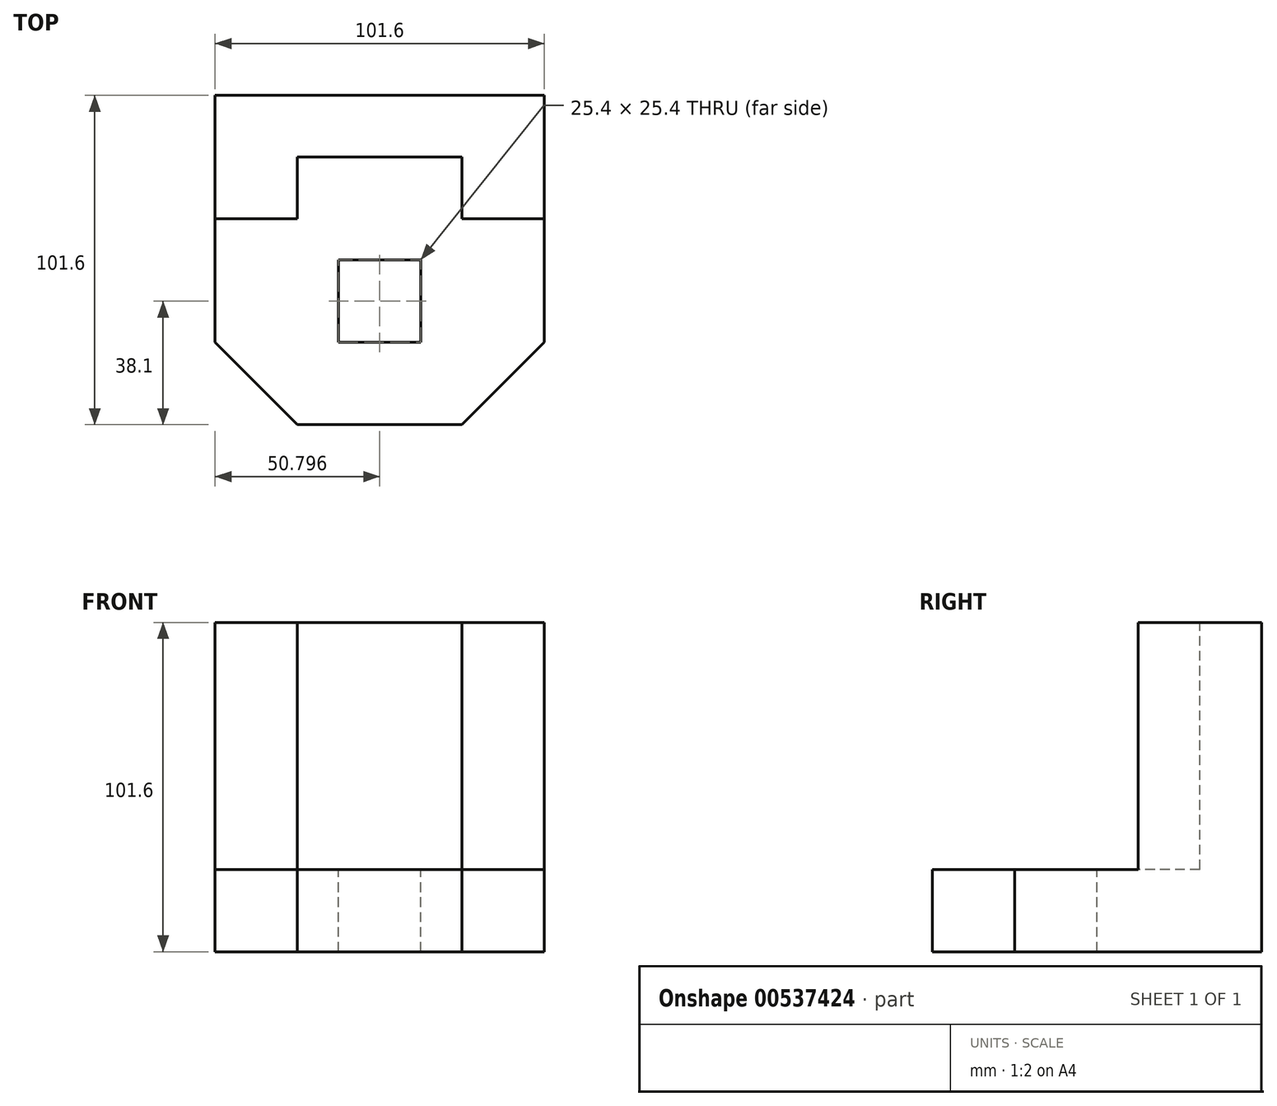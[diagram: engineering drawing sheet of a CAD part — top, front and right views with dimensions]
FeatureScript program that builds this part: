
annotation { "Feature Type Name" : "Feature", "Feature Type Description" : "" }
export const myFeature = defineFeature(function(context is Context, id is Id, definition is map)
    precondition{}
    {
        {
            var Q0;
            Q0=qCreatedBy(makeId("Front.planeOp"),FACE);
            var sketch = newSketch(context, id + "F0", { "sketchPlane" : qUnion([Q0])});
            skLineSegment(sketch, "E0.bottom", {"start": v(-35.7, 31.53) * mm, "end": v(65.9, 31.53) * mm});
            skLineSegment(sketch, "E0.top", {"start": v(-35.7, -70.07) * mm, "end": v(65.9, -70.07) * mm});
            skLineSegment(sketch, "E0.left", {"start": v(-35.7, 31.53) * mm, "end": v(-35.7, -70.07) * mm});
            skLineSegment(sketch, "E0.right", {"start": v(65.9, 31.53) * mm, "end": v(65.9, -70.07) * mm});
            skSolve(sketch);
        }
        {
            var Q0;
            Q0=makeQuery(id+"F0.imprint","IMPRINT",FACE,{"disambiguationData":[TD([[makeQuery(id+"F0.imprint","IMPRINT",EDGE,{"derivedFrom":sQuery(id+"F0.wireOp",EDGE,"E0.bottom")}),-1.0]])]});
            extrude(context, id + "F1", {"entities" : qUnion([Q0]), "depth" : 101.6 * mm, "offsetDistance" : 25.4 * mm});
        }
        {
            var Q0;
            Q0=makeQuery(id+"F1.opExtrude","CAP_FACE",FACE,{"disambiguationData":[OSD([sQuery(id+"F0.wireOp",EDGE,"E0.bottom"),sQuery(id+"F0.wireOp",EDGE,"E0.top"),sQuery(id+"F0.wireOp",EDGE,"E0.left"),sQuery(id+"F0.wireOp",EDGE,"E0.right")])],"isStart":false});
            var sketch = newSketch(context, id + "F2", { "sketchPlane" : qUnion([Q0])});
            skLineSegment(sketch, "E1.bottom", {"start": v(-35.7, 31.53) * mm, "end": v(65.9, 31.53) * mm});
            skLineSegment(sketch, "E1.top", {"start": v(-35.7, -44.67) * mm, "end": v(65.9, -44.67) * mm});
            skLineSegment(sketch, "E1.left", {"start": v(-35.7, 31.53) * mm, "end": v(-35.7, -44.67) * mm});
            skLineSegment(sketch, "E1.right", {"start": v(65.9, 31.53) * mm, "end": v(65.9, -44.67) * mm});
            skSolve(sketch);
        }
        {
            var Q0;
            Q0 = qSketchRegion(id + "F2", true);
            extrude(context, id + "F3", {"entities" : qUnion([Q0]), "operationType" : NewBodyOperationType.REMOVE, "oppositeDirection" : true, "depth" : 63.5 * mm, "offsetDistance" : 25.4 * mm});
        }
        {
            var Q0;
            Q0=makeQuery(id+"F1.opExtrude","SWEPT_FACE",FACE,{"disambiguationData":[OSD([sQuery(id+"F0.wireOp",EDGE,"E0.bottom")])]});
            var sketch = newSketch(context, id + "F4", { "sketchPlane" : qUnion([Q0])});
            skLineSegment(sketch, "E2.bottom", {"start": v(-35.7, 0) * mm, "end": v(-10.3, 0) * mm});
            skLineSegment(sketch, "E2.top", {"start": v(-35.7, -38.1) * mm, "end": v(-10.3, -38.1) * mm});
            skLineSegment(sketch, "E2.left", {"start": v(-35.7, 0) * mm, "end": v(-35.7, -38.1) * mm});
            skLineSegment(sketch, "E2.right", {"start": v(-10.3, 0) * mm, "end": v(-10.3, -38.1) * mm});
            skLineSegment(sketch, "E3.bottom", {"start": v(65.9, 0) * mm, "end": v(40.5, 0) * mm});
            skLineSegment(sketch, "E3.top", {"start": v(65.9, -38.1) * mm, "end": v(40.5, -38.1) * mm});
            skLineSegment(sketch, "E3.left", {"start": v(65.9, 0) * mm, "end": v(65.9, -38.1) * mm});
            skLineSegment(sketch, "E3.right", {"start": v(40.5, 0) * mm, "end": v(40.5, -38.1) * mm});
            skLineSegment(sketch, "E4.bottom", {"start": v(-35.7, -38.1) * mm, "end": v(65.9, -38.1) * mm});
            skLineSegment(sketch, "E4.top", {"start": v(-35.7, -19.05) * mm, "end": v(65.9, -19.05) * mm});
            skLineSegment(sketch, "E4.left", {"start": v(-35.7, -38.1) * mm, "end": v(-35.7, -19.05) * mm});
            skLineSegment(sketch, "E4.right", {"start": v(65.9, -38.1) * mm, "end": v(65.9, -19.05) * mm});
            skSolve(sketch);
        }
        {
            var Q0;
            {var subQ0=sQuery(id+"F4.wireOp",EDGE,"E4.bottom");var subQ1=sQuery(id+"F4.wireOp",EDGE,"E2.right");var subQ2=makeQuery(id+"F4.imprint","INTERSECT",VERTEX,{"derivedFrom":[subQ1,subQ0]});Q0=makeQuery(id+"F4.imprint","IMPRINT",FACE,{"disambiguationData":[TD([[makeQuery(id+"F4.imprint","IMPRINT",EDGE,{"disambiguationData":[TD([[subQ2,1.0]])],"derivedFrom":subQ1}),1.0]])]});}
            extrude(context, id + "F5", {"entities" : qUnion([Q0]), "operationType" : NewBodyOperationType.REMOVE, "oppositeDirection" : true, "depth" : 76.2 * mm, "offsetDistance" : 25.4 * mm});
        }
        {
            var Q0;
            Q0=makeQuery(id+"F5.boolean.opBoolean","MERGE",FACE,{"derivedFrom":[makeQuery(id+"F3.boolean.opBoolean","COPY",FACE,{"derivedFrom":makeQuery(id+"F3.opExtrude","SWEPT_FACE",FACE,{"disambiguationData":[OSD([sQuery(id+"F2.wireOp",EDGE,"E1.top")])]})}),makeQuery(id+"F5.opExtrude","CAP_FACE",FACE,{"disambiguationData":[OSD([sQuery(id+"F4.wireOp",EDGE,"E2.right"),sQuery(id+"F4.wireOp",EDGE,"E3.right"),sQuery(id+"F4.wireOp",EDGE,"E4.bottom"),sQuery(id+"F4.wireOp",EDGE,"E4.top")])],"isStart":false})]});
            var sketch = newSketch(context, id + "F6", { "sketchPlane" : qUnion([Q0])});
            skLineSegment(sketch, "E5.bottom", {"start": v(-35.7, -101.6) * mm, "end": v(-10.3, -101.6) * mm});
            skLineSegment(sketch, "E5.top", {"start": v(-35.7, -76.2) * mm, "end": v(-10.3, -76.2) * mm});
            skLineSegment(sketch, "E5.left", {"start": v(-35.7, -101.6) * mm, "end": v(-35.7, -76.2) * mm});
            skLineSegment(sketch, "E5.right", {"start": v(-10.3, -101.6) * mm, "end": v(-10.3, -76.2) * mm});
            skLineSegment(sketch, "E6.bottom", {"start": v(65.9, -101.6) * mm, "end": v(40.5, -101.6) * mm});
            skLineSegment(sketch, "E6.top", {"start": v(65.9, -76.2) * mm, "end": v(40.5, -76.2) * mm});
            skLineSegment(sketch, "E6.left", {"start": v(65.9, -101.6) * mm, "end": v(65.9, -76.2) * mm});
            skLineSegment(sketch, "E6.right", {"start": v(40.5, -101.6) * mm, "end": v(40.5, -76.2) * mm});
            skLineSegment(sketch, "E7", {"start": v(-35.7, -76.2) * mm, "end": v(-10.3, -101.6) * mm});
            skLineSegment(sketch, "E8", {"start": v(40.5, -101.6) * mm, "end": v(65.9, -76.2) * mm});
            skSolve(sketch);
        }
        {
            var Q0;
            Q0=makeQuery(id+"F6.imprint","IMPRINT",FACE,{"disambiguationData":[TD([[makeQuery(id+"F6.imprint","IMPRINT",EDGE,{"derivedFrom":sQuery(id+"F6.wireOp",EDGE,"E5.bottom")}),1.0]])]});
            var Q1;
            Q1=makeQuery(id+"F6.imprint","IMPRINT",FACE,{"disambiguationData":[TD([[makeQuery(id+"F6.imprint","IMPRINT",EDGE,{"derivedFrom":sQuery(id+"F6.wireOp",EDGE,"E6.bottom")}),1.0]])]});
            extrude(context, id + "F7", {"entities" : qUnion([Q0, Q1]), "operationType" : NewBodyOperationType.REMOVE, "oppositeDirection" : true, "depth" : 25.4 * mm, "offsetDistance" : 25.4 * mm});
        }
        {
            var Q0;
            Q0=makeQuery(id+"F5.boolean.opBoolean","MERGE",FACE,{"derivedFrom":[makeQuery(id+"F3.boolean.opBoolean","COPY",FACE,{"derivedFrom":makeQuery(id+"F3.opExtrude","SWEPT_FACE",FACE,{"disambiguationData":[OSD([sQuery(id+"F2.wireOp",EDGE,"E1.top")])]})}),makeQuery(id+"F5.opExtrude","CAP_FACE",FACE,{"disambiguationData":[OSD([sQuery(id+"F4.wireOp",EDGE,"E2.right"),sQuery(id+"F4.wireOp",EDGE,"E3.right"),sQuery(id+"F4.wireOp",EDGE,"E4.bottom"),sQuery(id+"F4.wireOp",EDGE,"E4.top")])],"isStart":false})]});
            var sketch = newSketch(context, id + "F8", { "sketchPlane" : qUnion([Q0])});
            skLineSegment(sketch, "E9", {"start": v(-10.3, -101.6) * mm, "end": v(2.4, -101.6) * mm});
            skLineSegment(sketch, "E10", {"start": v(40.5, -101.6) * mm, "end": v(27.8, -101.6) * mm});
            skLineSegment(sketch, "E11", {"start": v(65.9, -38.1) * mm, "end": v(65.9, -50.8) * mm});
            skLineSegment(sketch, "E12", {"start": v(-35.7, -38.1) * mm, "end": v(-35.7, -50.8) * mm});
            skLineSegment(sketch, "E13", {"start": v(-35.7, -50.8) * mm, "end": v(65.9, -50.8) * mm});
            skLineSegment(sketch, "E14", {"start": v(27.8, -101.6) * mm, "end": v(27.8, -19.05) * mm});
            skLineSegment(sketch, "E15", {"start": v(2.4, -101.6) * mm, "end": v(2.4, -19.05) * mm});
            skLineSegment(sketch, "E16", {"start": v(65.9, -76.2) * mm, "end": v(-35.7, -76.2) * mm});
            skSolve(sketch);
        }
        {
            var Q0;
            Q0 = qSketchRegion(id + "F8", true);
            extrude(context, id + "F9", {"entities" : qUnion([Q0]), "operationType" : NewBodyOperationType.REMOVE, "oppositeDirection" : true, "depth" : 25.4 * mm, "offsetDistance" : 25.4 * mm});
        }
    });
